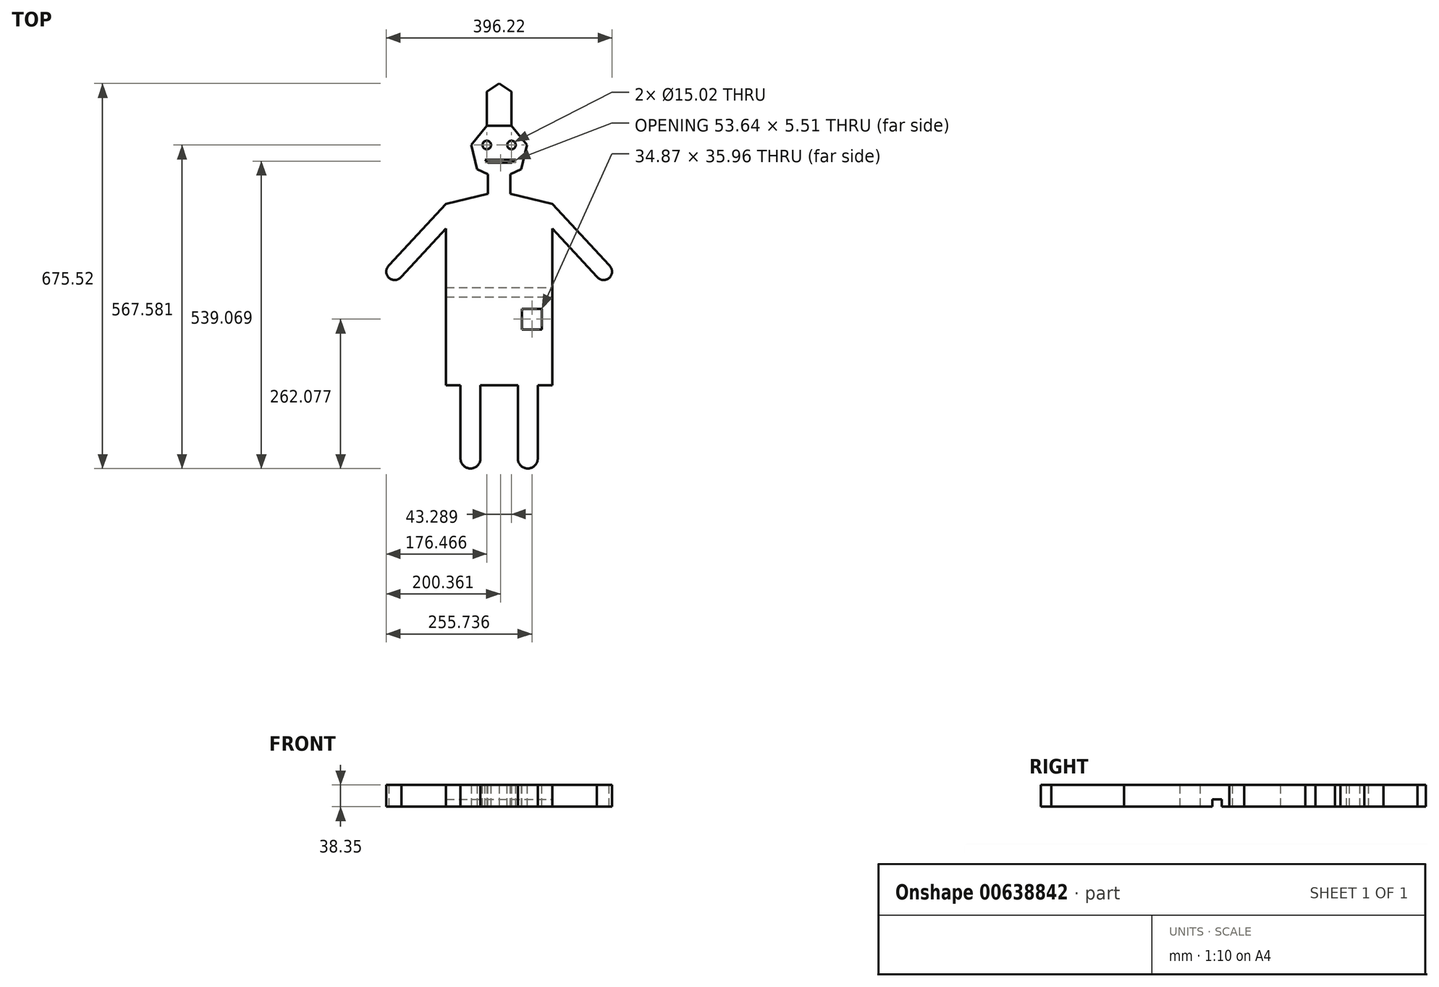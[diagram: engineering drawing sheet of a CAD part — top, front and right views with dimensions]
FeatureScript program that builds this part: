
annotation { "Feature Type Name" : "Feature", "Feature Type Description" : "" }
export const myFeature = defineFeature(function(context is Context, id is Id, definition is map)
    precondition{}
    {
        {
            var Q0;
            Q0=qCreatedBy(makeId("Top.planeOp"),FACE);
            var sketch = newSketch(context, id + "F0", { "sketchPlane" : qUnion([Q0])});
            skCircle(sketch, "E0.cCircle", {"center": v(0, 0) * mm, "radius": 44.94 * mm, "construction": true});
            skLineSegment(sketch, "E0.0", {"start": v(-21.64, 44.94) * mm, "end": v(21.64, 44.94) * mm});
            skLineSegment(sketch, "E0.1", {"start": v(21.64, 44.94) * mm, "end": v(48.63, 11.1) * mm});
            skLineSegment(sketch, "E0.2", {"start": v(48.63, 11.1) * mm, "end": v(39, -31.1) * mm});
            skLineSegment(sketch, "E0.3", {"start": v(39, -31.1) * mm, "end": v(0, -49.89) * mm});
            skLineSegment(sketch, "E0.4", {"start": v(0, -49.89) * mm, "end": v(-39, -31.1) * mm});
            skLineSegment(sketch, "E0.5", {"start": v(-39, -31.1) * mm, "end": v(-48.63, 11.1) * mm});
            skLineSegment(sketch, "E0.6", {"start": v(-48.63, 11.1) * mm, "end": v(-21.64, 44.94) * mm});
            skPoint(sketch, "E0.0.midPoint", {"position": v(0, 44.94) * mm});
            skSolve(sketch);
        }
        {
            var Q0;
            Q0=makeQuery(id+"F0.imprint","IMPRINT",FACE,{"disambiguationData":[TD([[makeQuery(id+"F0.imprint","IMPRINT",EDGE,{"derivedFrom":sQuery(id+"F0.wireOp",EDGE,"E0.0")}),-1.0]])]});
            extrude(context, id + "F1", {"entities" : qUnion([Q0]), "depth" : 12.7 * mm, "offsetDistance" : 25.4 * mm});
        }
        {
            var Q0;
            Q0=makeQuery(id+"F1.opExtrude","CAP_FACE",FACE,{"disambiguationData":[OSD([sQuery(id+"F0.wireOp",EDGE,"E0.0"),sQuery(id+"F0.wireOp",EDGE,"E0.1"),sQuery(id+"F0.wireOp",EDGE,"E0.2"),sQuery(id+"F0.wireOp",EDGE,"E0.3"),sQuery(id+"F0.wireOp",EDGE,"E0.4"),sQuery(id+"F0.wireOp",EDGE,"E0.5"),sQuery(id+"F0.wireOp",EDGE,"E0.6")])],"isStart":false});
            var sketch = newSketch(context, id + "F2", { "sketchPlane" : qUnion([Q0])});
            skCircle(sketch, "E1", {"center": v(-21.64, 11.1) * mm, "radius": 7.51 * mm});
            skCircle(sketch, "E2", {"center": v(21.64, 11.1) * mm, "radius": 7.51 * mm});
            skLineSegment(sketch, "E3", {"start": v(-17.3, -20.16) * mm, "end": v(19.55, -20.16) * mm});
            skLineSegment(sketch, "E4", {"start": v(23.33, -18.92) * mm, "end": v(29.07, -14.66) * mm});
            skLineSegment(sketch, "E5", {"start": v(-22.4, -17.6) * mm, "end": v(-24.57, -14.66) * mm});
            skLineSegment(sketch, "E6", {"start": v(-24.57, -14.66) * mm, "end": v(29.07, -14.66) * mm});
            skPoint(sketch, "E7.visualSharp", {"position": v(-20.49, -20.16) * mm});
            skArc(sketch, "E7.filletArc", {"start": v(-22.4, -17.6) * mm, "mid": v(-20.15, -19.49) * mm, "end": v(-17.3, -20.16) * mm});
            skPoint(sketch, "E8.visualSharp", {"position": v(21.64, -20.16) * mm});
            skArc(sketch, "E8.filletArc", {"start": v(19.55, -20.16) * mm, "mid": v(21.54, -19.84) * mm, "end": v(23.33, -18.92) * mm});
            skSolve(sketch);
        }
        {
            var Q0;
            Q0 = qSketchRegion(id + "F2", true);
            extrude(context, id + "F3", {"entities" : qUnion([Q0]), "operationType" : NewBodyOperationType.REMOVE, "endBound" : BoundingType.THROUGH_ALL, "oppositeDirection" : true, "depth" : 25.4 * mm, "offsetDistance" : 25.4 * mm});
        }
        {
            var Q0;
            Q0=makeQuery(id+"F1.opExtrude","CAP_FACE",FACE,{"disambiguationData":[OSD([sQuery(id+"F0.wireOp",EDGE,"E0.0"),sQuery(id+"F0.wireOp",EDGE,"E0.1"),sQuery(id+"F0.wireOp",EDGE,"E0.2"),sQuery(id+"F0.wireOp",EDGE,"E0.3"),sQuery(id+"F0.wireOp",EDGE,"E0.4"),sQuery(id+"F0.wireOp",EDGE,"E0.5"),sQuery(id+"F0.wireOp",EDGE,"E0.6")])],"isStart":false});
            var sketch = newSketch(context, id + "F4", { "sketchPlane" : qUnion([Q0])});
            skLineSegment(sketch, "E9", {"start": v(-19.5, -40.5) * mm, "end": v(-19.5, -74.57) * mm});
            skLineSegment(sketch, "E10", {"start": v(19.5, -40.5) * mm, "end": v(19.5, -74.57) * mm});
            skLineSegment(sketch, "E11", {"start": v(19.5, -74.57) * mm, "end": v(-19.5, -74.57) * mm});
            skLineSegment(sketch, "E12", {"start": v(-19.5, -74.57) * mm, "end": v(-93.58, -92.42) * mm});
            skLineSegment(sketch, "E13", {"start": v(19.5, -74.57) * mm, "end": v(93.58, -92.42) * mm});
            skLineSegment(sketch, "E14", {"start": v(-93.58, -92.42) * mm, "end": v(-93.58, -255.61) * mm});
            skLineSegment(sketch, "E15", {"start": v(93.58, -92.42) * mm, "end": v(93.58, -255.61) * mm});
            skLineSegment(sketch, "E16", {"start": v(-93.58, -255.61) * mm, "end": v(93.58, -255.61) * mm});
            skLineSegment(sketch, "E17", {"start": v(-93.58, -92.42) * mm, "end": v(-194.1, -201.05) * mm});
            skLineSegment(sketch, "E18", {"start": v(-172.54, -221.01) * mm, "end": v(-93.58, -135.69) * mm});
            skLineSegment(sketch, "E19", {"start": v(0, -74.57) * mm, "end": v(0, -368.65) * mm, "construction": true});
            skLineSegment(sketch, "E20", {"start": v(-93.58, -255.61) * mm, "end": v(-93.58, -410.44) * mm});
            skLineSegment(sketch, "E21", {"start": v(-93.58, -410.44) * mm, "end": v(0, -410.44) * mm});
            skLineSegment(sketch, "E22.MirrorCS", {"start": v(93.58, -92.42) * mm, "end": v(194.1, -201.05) * mm});
            skLineSegment(sketch, "E23.MirrorCS", {"start": v(172.54, -221.01) * mm, "end": v(93.58, -135.69) * mm});
            skLineSegment(sketch, "E24.MirrorCS", {"start": v(93.58, -255.61) * mm, "end": v(93.58, -410.44) * mm});
            skLineSegment(sketch, "E25.MirrorCS", {"start": v(93.58, -410.44) * mm, "end": v(0, -410.44) * mm});
            skLineSegment(sketch, "E26", {"start": v(40.2, -276.43) * mm, "end": v(40.2, -312.38) * mm});
            skLineSegment(sketch, "E27", {"start": v(40.2, -312.38) * mm, "end": v(75.06, -312.38) * mm});
            skLineSegment(sketch, "E28", {"start": v(75.06, -312.38) * mm, "end": v(75.06, -276.43) * mm});
            skLineSegment(sketch, "E29", {"start": v(75.06, -276.43) * mm, "end": v(40.2, -276.43) * mm});
            skFitSpline(sketch, "E30", {"points": [v(-56.54, -83.5) * mm, v(0, -131.51) * mm, v(56.54, -83.5) * mm], "startDerivative": vector(114.5, -145.55) * mm, "endDerivative": vector(114.5, 145.55) * mm});
            skLineSegment(sketch, "E31", {"start": v(-67.67, -410.44) * mm, "end": v(-67.67, -539) * mm});
            skLineSegment(sketch, "E32", {"start": v(-32.8, -539) * mm, "end": v(-32.8, -410.44) * mm});
            skLineSegment(sketch, "E33.MirrorCS", {"start": v(32.8, -539) * mm, "end": v(32.8, -410.44) * mm});
            skLineSegment(sketch, "E34.MirrorCS", {"start": v(67.67, -410.44) * mm, "end": v(67.67, -539) * mm});
            skArc(sketch, "E35", {"start": v(-67.67, -537.92) * mm, "mid": v(-50.24, -556.48) * mm, "end": v(-32.8, -537.92) * mm});
            skArc(sketch, "E36.MirrorCS", {"start": v(67.67, -537.92) * mm, "mid": v(50.24, -556.48) * mm, "end": v(32.8, -537.92) * mm});
            skArc(sketch, "E37", {"start": v(-192.94, -199.79) * mm, "mid": v(-193.37, -221.9) * mm, "end": v(-171.37, -219.75) * mm});
            skArc(sketch, "E38.MirrorC", {"start": v(192.94, -199.79) * mm, "mid": v(193.37, -221.9) * mm, "end": v(171.37, -219.75) * mm});
            skPoint(sketch, "E39.orphan", {"position": v(194.1, -201.05) * mm});
            skPoint(sketch, "E40.MirrorCS.end.orphan", {"position": v(172.54, -221.01) * mm});
            skLineSegment(sketch, "E41", {"start": v(-93.58, -255.61) * mm, "end": v(-93.58, -239.13) * mm});
            skLineSegment(sketch, "E42", {"start": v(-93.58, -239.13) * mm, "end": v(93.58, -239.13) * mm});
            skLineSegment(sketch, "E43", {"start": v(93.58, -239.13) * mm, "end": v(93.58, -255.61) * mm});
            skSolve(sketch);
        }
        {
            var Q0;
            Q0 = qSketchRegion(id + "F4", true);
            var Q1;
            {var subQ4=sQuery(id+"F4.wireOp",EDGE,"E9");Q1=makeQuery(id+"F4.imprint","IMPRINT",FACE,{"disambiguationData":[TD([[makeQuery(id+"F4.imprint","IMPRINT",EDGE,{"derivedFrom":subQ4}),1.0]])]});}
            extrude(context, id + "F5", {"entities" : qUnion([Q0, Q1]), "operationType" : NewBodyOperationType.ADD, "oppositeDirection" : true, "depth" : 12.7 * mm, "offsetDistance" : 25.4 * mm});
        }
        {
            var Q0;
            Q0 = qSketchRegion(id + "F4", true);
            var Q1;
            {var subQ0=sQuery(id+"F0.wireOp",EDGE,"E0.4");var subQ1=sQuery(id+"F0.wireOp",EDGE,"E0.3");Q1=makeQuery(id+"F5.boolean.opBoolean","MERGE",FACE,{"derivedFrom":[makeQuery(id+"F1.opExtrude","CAP_FACE",FACE,{"disambiguationData":[OSD([sQuery(id+"F0.wireOp",EDGE,"E0.0"),sQuery(id+"F0.wireOp",EDGE,"E0.1"),sQuery(id+"F0.wireOp",EDGE,"E0.2"),subQ1,subQ0,sQuery(id+"F0.wireOp",EDGE,"E0.5"),sQuery(id+"F0.wireOp",EDGE,"E0.6")])],"isStart":false}),makeQuery(id+"F5.opExtrude","CAP_FACE",FACE,{"disambiguationData":[OSD([subQ1,subQ0,sQuery(id+"F4.wireOp",EDGE,"E9"),sQuery(id+"F4.wireOp",EDGE,"E10"),sQuery(id+"F4.wireOp",EDGE,"E12"),sQuery(id+"F4.wireOp",EDGE,"E13"),sQuery(id+"F4.wireOp",EDGE,"E14"),sQuery(id+"F4.wireOp",EDGE,"E15"),sQuery(id+"F4.wireOp",EDGE,"E17"),sQuery(id+"F4.wireOp",EDGE,"E18"),sQuery(id+"F4.wireOp",EDGE,"E20"),sQuery(id+"F4.wireOp",EDGE,"E21"),sQuery(id+"F4.wireOp",EDGE,"E22.MirrorCS"),sQuery(id+"F4.wireOp",EDGE,"E23.MirrorCS"),sQuery(id+"F4.wireOp",EDGE,"E24.MirrorCS"),sQuery(id+"F4.wireOp",EDGE,"E25.MirrorCS"),sQuery(id+"F4.wireOp",EDGE,"E26"),sQuery(id+"F4.wireOp",EDGE,"E27"),sQuery(id+"F4.wireOp",EDGE,"E28"),sQuery(id+"F4.wireOp",EDGE,"E29"),sQuery(id+"F4.wireOp",EDGE,"E31"),sQuery(id+"F4.wireOp",EDGE,"E32"),sQuery(id+"F4.wireOp",EDGE,"E33.MirrorCS"),sQuery(id+"F4.wireOp",EDGE,"E34.MirrorCS"),sQuery(id+"F4.wireOp",EDGE,"E35"),sQuery(id+"F4.wireOp",EDGE,"E36.MirrorCS"),sQuery(id+"F4.wireOp",EDGE,"E37"),sQuery(id+"F4.wireOp",EDGE,"E38.MirrorC"),sQuery(id+"F4.wireOp",EDGE,"E41"),sQuery(id+"F4.wireOp",EDGE,"E43")])],"isStart":true})]});}
            extrude(context, id + "F6", {"entities" : qUnion([Q0, Q1]), "operationType" : NewBodyOperationType.ADD, "depth" : 25.4 * mm, "offsetDistance" : 25.4 * mm});
        }
        {
            var Q0;
            Q0=makeQuery(id+"F4.imprint","IMPRINT",FACE,{"disambiguationData":[TD([[makeQuery(id+"F4.imprint","IMPRINT",EDGE,{"derivedFrom":sQuery(id+"F4.wireOp",EDGE,"E16")}),1.0]])]});
            extrude(context, id + "F7", {"entities" : qUnion([Q0]), "operationType" : NewBodyOperationType.REMOVE, "oppositeDirection" : true, "depth" : 12.7 * mm, "offsetDistance" : 25.4 * mm});
        }
        {
            var Q0;
            {var subQ5=sQuery(id+"F4.wireOp",EDGE,"E22.MirrorCS");var subQ6=sQuery(id+"F0.wireOp",EDGE,"E0.0");var subQ8=sQuery(id+"F4.wireOp",EDGE,"E18");var subQ9=sQuery(id+"F4.wireOp",EDGE,"E41");var subQ10=sQuery(id+"F4.wireOp",EDGE,"E20");var subQ12=sQuery(id+"F4.wireOp",EDGE,"E14");var subQ14=sQuery(id+"F0.wireOp",EDGE,"E0.6");var subQ15=sQuery(id+"F4.wireOp",EDGE,"E15");var subQ16=sQuery(id+"F4.wireOp",EDGE,"E13");var subQ21=sQuery(id+"F4.wireOp",EDGE,"E10");var subQ22=sQuery(id+"F0.wireOp",EDGE,"E0.5");var subQ24=sQuery(id+"F4.wireOp",EDGE,"E23.MirrorCS");var subQ25=sQuery(id+"F0.wireOp",EDGE,"E0.1");var subQ26=sQuery(id+"F4.wireOp",EDGE,"E17");var subQ27=sQuery(id+"F4.wireOp",EDGE,"E12");var subQ30=sQuery(id+"F4.wireOp",EDGE,"E9");var subQ31=sQuery(id+"F0.wireOp",EDGE,"E0.4");var subQ33=sQuery(id+"F0.wireOp",EDGE,"E0.3");var subQ34=sQuery(id+"F0.wireOp",EDGE,"E0.2");var subQ35=sQuery(id+"F4.wireOp",EDGE,"E43");var subQ36=sQuery(id+"F4.wireOp",EDGE,"E24.MirrorCS");var subQ38=sQuery(id+"F4.wireOp",EDGE,"E37");var subQ39=sQuery(id+"F4.wireOp",EDGE,"E38.MirrorC");Q0=makeQuery(id+"F7.boolean.opBoolean","SPLIT",FACE,{"disambiguationData":[TD([makeQuery(id+"F1.opExtrude","SWEPT_FACE",FACE,{"disambiguationData":[OSD([subQ6])]})])],"derivedFrom":makeQuery(id+"F5.boolean.opBoolean","MERGE",FACE,{"derivedFrom":[makeQuery(id+"F1.opExtrude","CAP_FACE",FACE,{"disambiguationData":[OSD([subQ6,subQ25,subQ34,subQ33,subQ31,subQ22,subQ14])],"isStart":true}),makeQuery(id+"F5.opExtrude","CAP_FACE",FACE,{"disambiguationData":[OSD([subQ33,subQ31,subQ30,subQ21,subQ27,subQ16,subQ12,subQ15,subQ26,subQ8,subQ10,sQuery(id+"F4.wireOp",EDGE,"E21"),subQ5,subQ24,subQ36,sQuery(id+"F4.wireOp",EDGE,"E25.MirrorCS"),sQuery(id+"F4.wireOp",EDGE,"E26"),sQuery(id+"F4.wireOp",EDGE,"E27"),sQuery(id+"F4.wireOp",EDGE,"E28"),sQuery(id+"F4.wireOp",EDGE,"E29"),sQuery(id+"F4.wireOp",EDGE,"E31"),sQuery(id+"F4.wireOp",EDGE,"E32"),sQuery(id+"F4.wireOp",EDGE,"E33.MirrorCS"),sQuery(id+"F4.wireOp",EDGE,"E34.MirrorCS"),sQuery(id+"F4.wireOp",EDGE,"E35"),sQuery(id+"F4.wireOp",EDGE,"E36.MirrorCS"),subQ38,subQ39,subQ9,subQ35])],"isStart":false})]})});}
            var sketch = newSketch(context, id + "F8", { "sketchPlane" : qUnion([Q0])});
            skLineSegment(sketch, "E44", {"start": v(21.64, -44.94) * mm, "end": v(21.64, -104.62) * mm});
            skLineSegment(sketch, "E45", {"start": v(21.64, -104.62) * mm, "end": v(0, -119.04) * mm});
            skLineSegment(sketch, "E46", {"start": v(0, -119.04) * mm, "end": v(-21.64, -104.62) * mm});
            skLineSegment(sketch, "E47", {"start": v(-21.64, -104.62) * mm, "end": v(-21.64, -44.94) * mm});
            skLineSegment(sketch, "E48", {"start": v(-21.64, -44.94) * mm, "end": v(21.64, -44.94) * mm});
            skSolve(sketch);
        }
        {
            var Q0;
            Q0 = qSketchRegion(id + "F8", true);
            extrude(context, id + "F9", {"entities" : qUnion([Q0]), "operationType" : NewBodyOperationType.ADD, "oppositeDirection" : true, "depth" : 38.35 * mm, "offsetDistance" : 25.4 * mm});
        }
    });
